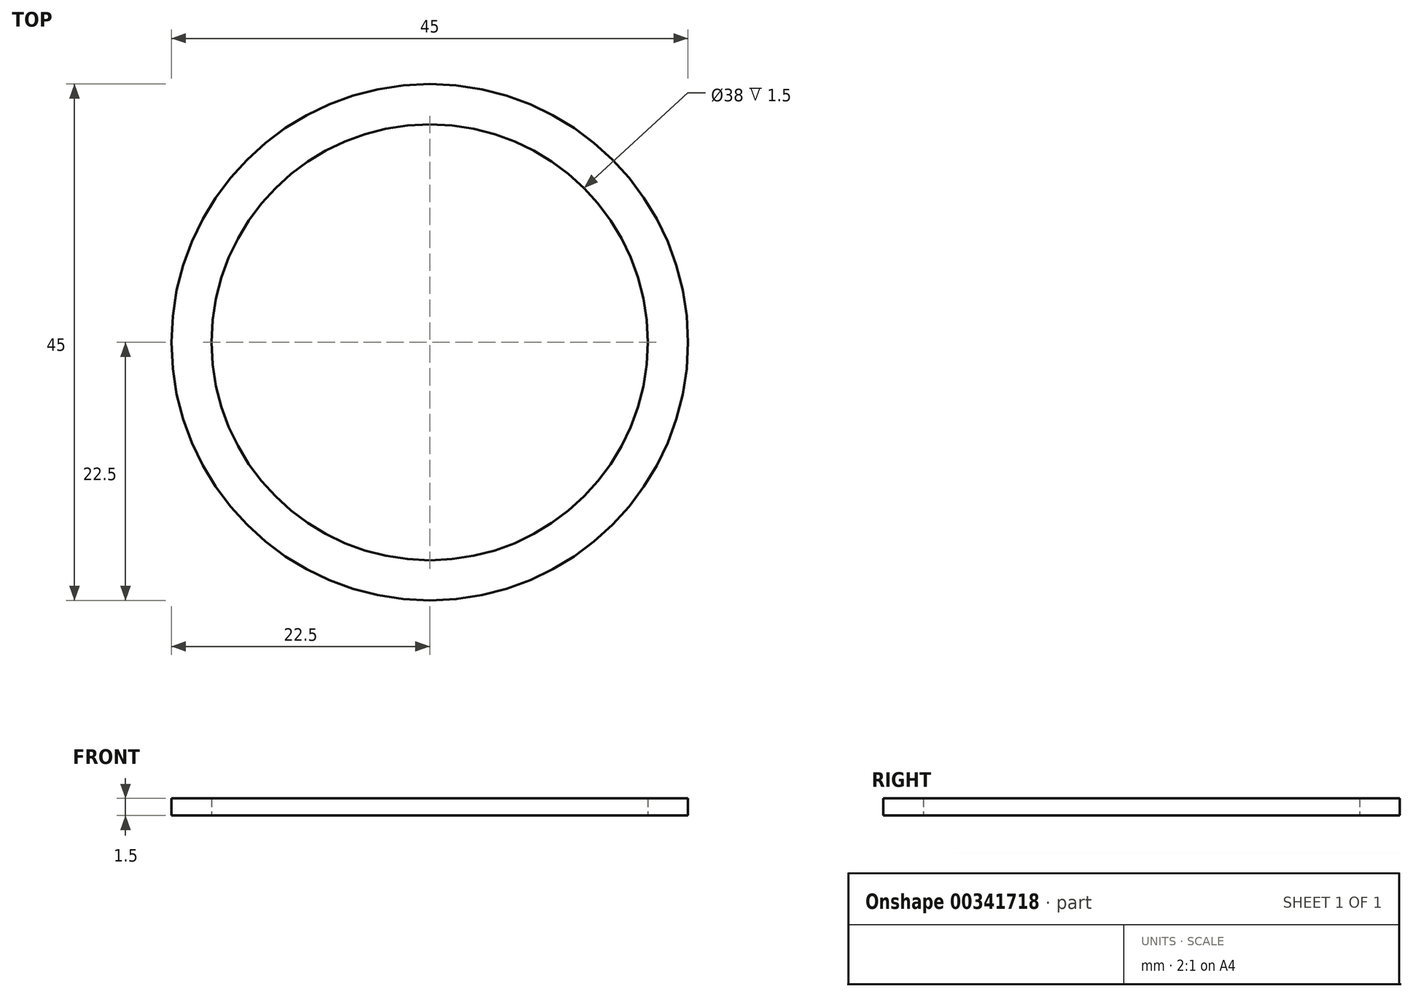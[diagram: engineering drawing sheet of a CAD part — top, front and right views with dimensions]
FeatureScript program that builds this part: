
annotation { "Feature Type Name" : "Feature", "Feature Type Description" : "" }
export const myFeature = defineFeature(function(context is Context, id is Id, definition is map)
    precondition{}
    {
        {
            var Q0;
            Q0=qCreatedBy(makeId("Top.planeOp"),FACE);
            var sketch = newSketch(context, id + "F0", { "sketchPlane" : qUnion([Q0])});
            skCircle(sketch, "E0", {"center": v(0, 0) * mm, "radius": 18 * mm});
            skCircle(sketch, "E1", {"center": v(0, 0) * mm, "radius": 22.5 * mm});
            skCircle(sketch, "E2", {"center": v(0, 0) * mm, "radius": 16 * mm});
            skCircle(sketch, "E3", {"center": v(0, 0) * mm, "radius": 19 * mm});
            skSolve(sketch);
        }
        {
            var Q0;
            Q0=makeQuery(id+"F0.imprint","IMPRINT",FACE,{"disambiguationData":[TD([[makeQuery(id+"F0.imprint","IMPRINT",EDGE,{"derivedFrom":sQuery(id+"F0.wireOp",EDGE,"E1")}),1.0]])]});
            extrude(context, id + "F1", {"entities" : qUnion([Q0]), "depth" : 1.5 * mm});
        }
    });
